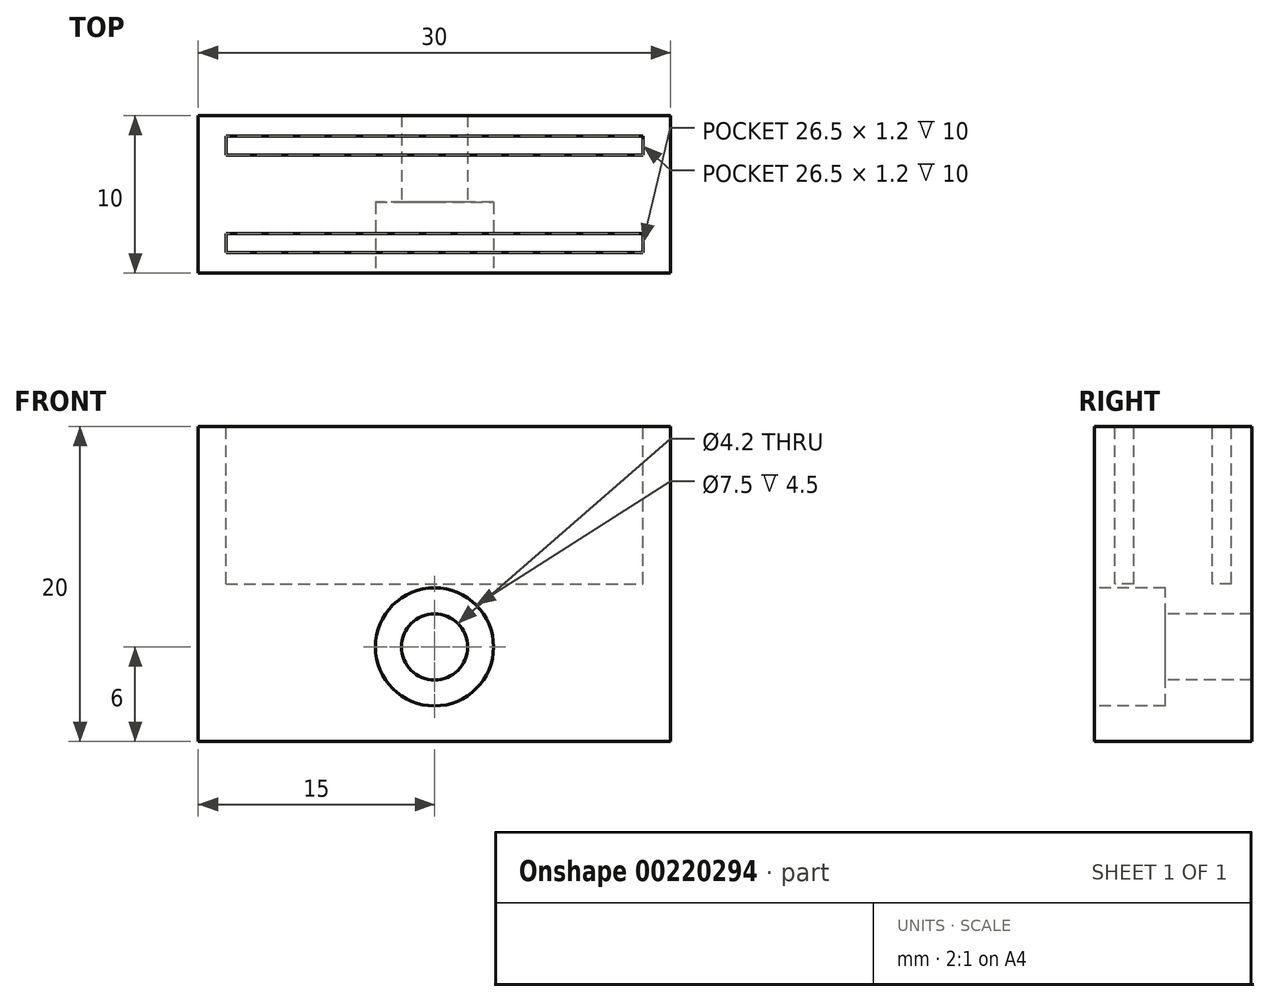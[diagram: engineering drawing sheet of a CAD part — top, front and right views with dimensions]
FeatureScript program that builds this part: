
annotation { "Feature Type Name" : "Feature", "Feature Type Description" : "" }
export const myFeature = defineFeature(function(context is Context, id is Id, definition is map)
    precondition{}
    {
        {
            var Q0;
            Q0=qCreatedBy(makeId("Top.planeOp"),FACE);
            var sketch = newSketch(context, id + "F0", { "sketchPlane" : qUnion([Q0])});
            skLineSegment(sketch, "E0.bottom", {"start": v(15, 5) * mm, "end": v(-15, 5) * mm});
            skLineSegment(sketch, "E0.top", {"start": v(15, -5) * mm, "end": v(-15, -5) * mm});
            skLineSegment(sketch, "E0.left", {"start": v(15, 5) * mm, "end": v(15, -5) * mm});
            skLineSegment(sketch, "E0.right", {"start": v(-15, 5) * mm, "end": v(-15, -5) * mm});
            skPoint(sketch, "E0.middle", {"position": v(0, 0) * mm});
            skSolve(sketch);
        }
        {
            var Q0;
            Q0=makeQuery(id+"F0.imprint","IMPRINT",FACE,{"disambiguationData":[TD([[makeQuery(id+"F0.imprint","IMPRINT",EDGE,{"derivedFrom":sQuery(id+"F0.wireOp",EDGE,"E0.bottom")}),1.0]])]});
            extrude(context, id + "F1", {"entities" : qUnion([Q0]), "depth" : 20 * mm});
        }
        {
            var Q0;
            Q0=makeQuery(id+"F1.opExtrude","SWEPT_FACE",FACE,{"disambiguationData":[OSD([sQuery(id+"F0.wireOp",EDGE,"E0.top")])]});
            var sketch = newSketch(context, id + "F2", { "sketchPlane" : qUnion([Q0])});
            skCircle(sketch, "E1", {"center": v(0, 6) * mm, "radius": 2.1 * mm});
            skSolve(sketch);
        }
        {
            var Q0;
            Q0 = qSketchRegion(id + "F2", true);
            extrude(context, id + "F3", {"entities" : qUnion([Q0]), "operationType" : NewBodyOperationType.REMOVE, "endBound" : BoundingType.UP_TO_NEXT, "oppositeDirection" : true, "depth" : 25 * mm});
        }
        {
            var Q0;
            Q0=makeQuery(id+"F1.opExtrude","CAP_FACE",FACE,{"disambiguationData":[OSD([sQuery(id+"F0.wireOp",EDGE,"E0.bottom"),sQuery(id+"F0.wireOp",EDGE,"E0.top"),sQuery(id+"F0.wireOp",EDGE,"E0.left"),sQuery(id+"F0.wireOp",EDGE,"E0.right")])],"isStart":false});
            var sketch = newSketch(context, id + "F4", { "sketchPlane" : qUnion([Q0])});
            skLineSegment(sketch, "E2.bottom", {"start": v(-13.25, 3.7) * mm, "end": v(13.25, 3.7) * mm});
            skLineSegment(sketch, "E2.top", {"start": v(-13.25, 2.5) * mm, "end": v(13.25, 2.5) * mm});
            skLineSegment(sketch, "E2.left", {"start": v(-13.25, 3.7) * mm, "end": v(-13.25, 2.5) * mm});
            skLineSegment(sketch, "E2.right", {"start": v(13.25, 3.7) * mm, "end": v(13.25, 2.5) * mm});
            skLineSegment(sketch, "E3.bottom", {"start": v(-13.25, -2.5) * mm, "end": v(13.25, -2.5) * mm});
            skLineSegment(sketch, "E3.top", {"start": v(-13.25, -3.7) * mm, "end": v(13.25, -3.7) * mm});
            skLineSegment(sketch, "E3.left", {"start": v(-13.25, -2.5) * mm, "end": v(-13.25, -3.7) * mm});
            skLineSegment(sketch, "E3.right", {"start": v(13.25, -2.5) * mm, "end": v(13.25, -3.7) * mm});
            skLineSegment(sketch, "E4", {"start": v(-13.25, -2.5) * mm, "end": v(-13.25, 2.5) * mm, "construction": true});
            skLineSegment(sketch, "E5", {"start": v(13.25, 2.5) * mm, "end": v(13.25, -2.5) * mm, "construction": true});
            skLineSegment(sketch, "E6", {"start": v(0, 2.5) * mm, "end": v(0, 0) * mm, "construction": true});
            skSolve(sketch);
        }
        {
            var Q0;
            Q0 = qSketchRegion(id + "F4", true);
            extrude(context, id + "F5", {"entities" : qUnion([Q0]), "operationType" : NewBodyOperationType.REMOVE, "oppositeDirection" : true, "depth" : 10 * mm});
        }
        {
            var Q0;
            Q0=makeQuery(id+"F1.opExtrude","SWEPT_FACE",FACE,{"disambiguationData":[OSD([sQuery(id+"F0.wireOp",EDGE,"E0.top")])]});
            var sketch = newSketch(context, id + "F6", { "sketchPlane" : qUnion([Q0])});
            skCircle(sketch, "E7", {"center": v(0, 6) * mm, "radius": 3.75 * mm});
            skSolve(sketch);
        }
        {
            var Q0;
            Q0 = qSketchRegion(id + "F6", true);
            extrude(context, id + "F7", {"entities" : qUnion([Q0]), "operationType" : NewBodyOperationType.REMOVE, "oppositeDirection" : true, "depth" : 4.5 * mm});
        }
    });
